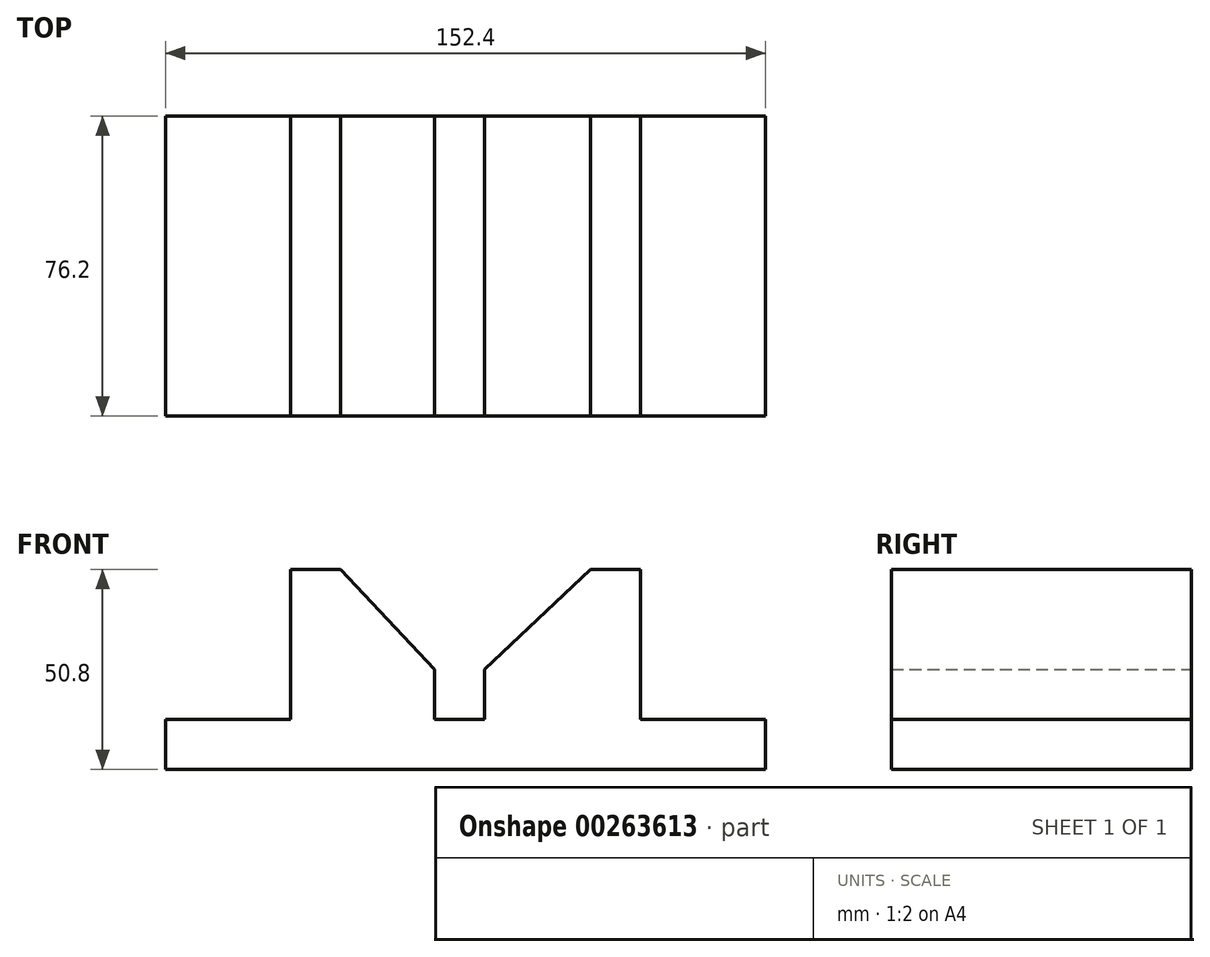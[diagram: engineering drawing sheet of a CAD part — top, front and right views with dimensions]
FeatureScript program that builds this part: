
annotation { "Feature Type Name" : "Feature", "Feature Type Description" : "" }
export const myFeature = defineFeature(function(context is Context, id is Id, definition is map)
    precondition{}
    {
        {
            var Q0;
            Q0=qCreatedBy(makeId("Front.planeOp"),FACE);
            var sketch = newSketch(context, id + "F0", { "sketchPlane" : qUnion([Q0])});
            skLineSegment(sketch, "E0", {"start": v(-127.03, -50.8) * mm, "end": v(25.37, -50.8) * mm});
            skLineSegment(sketch, "E1", {"start": v(25.37, -50.8) * mm, "end": v(25.37, -38.1) * mm});
            skLineSegment(sketch, "E2", {"start": v(25.37, -38.1) * mm, "end": v(-6.38, -38.1) * mm});
            skLineSegment(sketch, "E3", {"start": v(-6.38, -38.1) * mm, "end": v(-6.38, 0) * mm});
            skLineSegment(sketch, "E4", {"start": v(-6.38, 0) * mm, "end": v(-19.08, 0) * mm});
            skLineSegment(sketch, "E5", {"start": v(-127.03, -50.8) * mm, "end": v(-127.03, -38.1) * mm});
            skLineSegment(sketch, "E6", {"start": v(-127.03, -38.1) * mm, "end": v(-95.28, -38.1) * mm});
            skLineSegment(sketch, "E7", {"start": v(-95.28, -38.1) * mm, "end": v(-95.28, 0) * mm});
            skLineSegment(sketch, "E8", {"start": v(-95.28, 0) * mm, "end": v(-82.58, 0) * mm});
            skLineSegment(sketch, "E9", {"start": v(-45.98, -38.1) * mm, "end": v(-45.98, -25.4) * mm});
            skLineSegment(sketch, "E10", {"start": v(-45.98, -38.1) * mm, "end": v(-58.68, -38.1) * mm});
            skLineSegment(sketch, "E11", {"start": v(-58.68, -38.1) * mm, "end": v(-58.68, -25.4) * mm});
            skLineSegment(sketch, "E12", {"start": v(-58.68, -25.4) * mm, "end": v(-82.58, 0) * mm});
            skLineSegment(sketch, "E13", {"start": v(-19.08, 0) * mm, "end": v(-45.98, -25.4) * mm});
            skSolve(sketch);
        }
        {
            var Q0;
            Q0=makeQuery(id+"F0.imprint","IMPRINT",FACE,{"disambiguationData":[TD([[makeQuery(id+"F0.imprint","IMPRINT",EDGE,{"derivedFrom":sQuery(id+"F0.wireOp",EDGE,"E0")}),1.0]])]});
            extrude(context, id + "F1", {"entities" : qUnion([Q0]), "depth" : 76.2 * mm});
        }
    });
